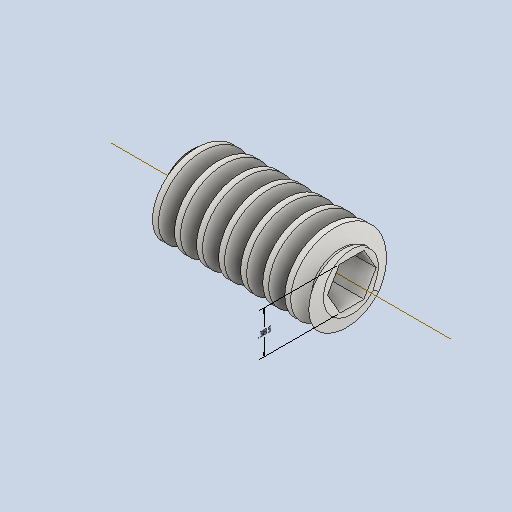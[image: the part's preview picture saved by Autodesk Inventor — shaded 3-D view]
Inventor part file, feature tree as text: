
AUTODESK INVENTOR PART (.ipt)
format: ipt  version: 2022.1 (Build 261234000, 234)  size: 426,496 bytes
history: native  units: mm (DEFAULTED — no unit token found)
features: other x8, extrude x2, chamfer x2, pattern_circular x2, sketch x2, thicken_offset x1
ambient origin geometry x6: Origin, XZ Plane, X Axis, Y Axis, Z Axis, Center Point
bodies: Solid1 (feature_tree)
feature tree (17):
  other  "Annotations"
  extrude  "Base Body"  Depth=19.404171mm
  chamfer  "Chamfer1"  [1 undecoded]
  chamfer  "Chamfer2"  Distance=1.294799mm
  other  "Tooth Sketch"
  other  "Left Tooth"
  pattern_circular  "Left Tooth Pattern"  [2 undecoded]
  other  "Tooth"
  pattern_circular  "Tooth Pattern"  [2 undecoded]
  extrude  "Extrusion2"  Depth=9.779mm
  thicken_offset  "Thicken1"
  other  "Base Body Sketch"
  sketch  "Sketch5"  dims[d4=40.0mm d5=19.404171mm]
  other  "Srf1"
  sketch  "Sketch6"  dims[d6=38.1mm d7=0.0mm d8=1.294799mm d9=3.557431mm d10=1.294799mm d11=3.557431mm d12=19.198622mm d14=3.1425mm d24=19.198622mm d25=22.86mm d26=1.27mm d27=6.144654mm d28=8.085071mm d29=9.799106mm d30=5.08mm d31=10.0mm d32=100.0mm d33=0.0mm d34=90.0deg d35=90.0deg d36=0.0mm d37=0.0mm d43=10.0mm d45=360.0deg d46=45.0deg d47=45.0deg d49=0.0mm d53=0.0mm d54=56.595498mm d55=0.0mm d56=0.0mm d57=16.170142mm d58=25.4mm d59=0.0mm d60=5.08mm d61=25.4mm d62=100.0mm d63=0.0mm d64=90.0deg d65=90.0deg d66=0.0mm d67=0.0mm d68=10.0mm d69=10.0mm d70=360.0deg d72=10.0mm d74=10.0mm d75=10.0mm d76=0.0mm d77=56.595498mm d78=9.525mm d79=0.0mm d80=0.0mm d81=0.127mm d82=0.127mm d83=2.865495mm d84=9.779mm]
  other  "Pitch Diameter"
  other  "Linear Dimension 1"
note: 5 required parameter values undecoded (feature->parameter linkage not recoverable at this tier; creation-order binding heuristic only, values carry confidence <= 0.55)
